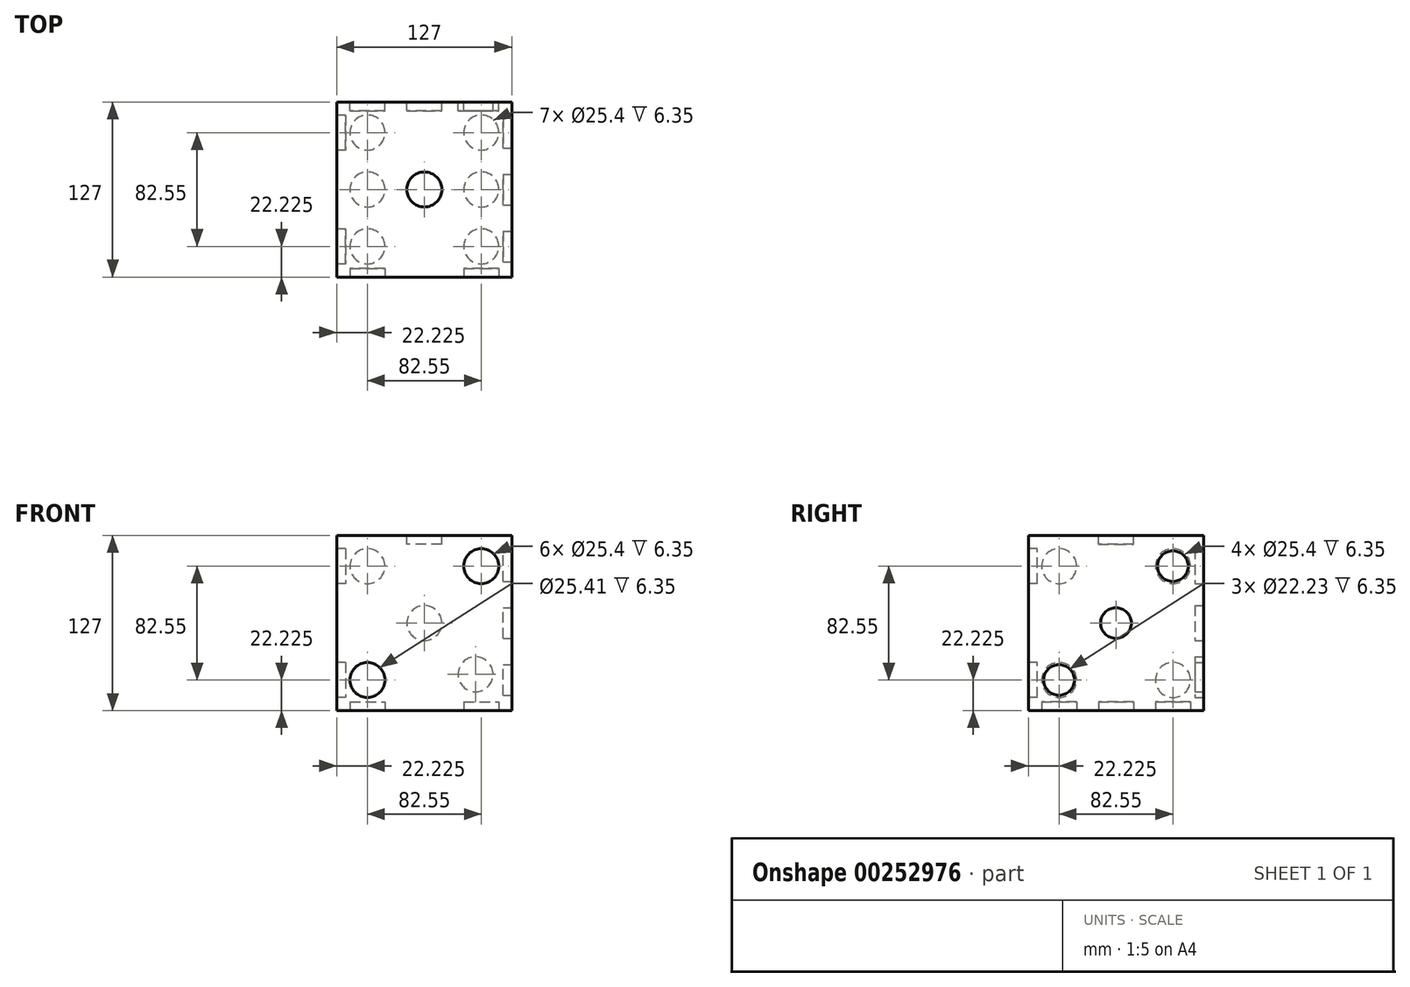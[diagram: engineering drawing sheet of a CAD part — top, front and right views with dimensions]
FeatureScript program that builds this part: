
annotation { "Feature Type Name" : "Feature", "Feature Type Description" : "" }
export const myFeature = defineFeature(function(context is Context, id is Id, definition is map)
    precondition{}
    {
        {
            var Q0;
            Q0=qCreatedBy(makeId("Top.planeOp"),FACE);
            var sketch = newSketch(context, id + "F0", { "sketchPlane" : qUnion([Q0])});
            skLineSegment(sketch, "E0.bottom", {"start": v(63.5, -63.5) * mm, "end": v(-63.5, -63.5) * mm});
            skLineSegment(sketch, "E0.top", {"start": v(63.5, 63.5) * mm, "end": v(-63.5, 63.5) * mm});
            skLineSegment(sketch, "E0.left", {"start": v(63.5, -63.5) * mm, "end": v(63.5, 63.5) * mm});
            skLineSegment(sketch, "E0.right", {"start": v(-63.5, -63.5) * mm, "end": v(-63.5, 63.5) * mm});
            skPoint(sketch, "E0.middle", {"position": v(0, 0) * mm});
            skSolve(sketch);
        }
        {
            var Q0;
            Q0 = qSketchRegion(id + "F0", true);
            extrude(context, id + "F1", {"entities" : qUnion([Q0]), "depth" : 127 * mm});
        }
        {
            var Q0;
            Q0=makeQuery(id+"F1.opExtrude","CAP_FACE",FACE,{"disambiguationData":[OSD([sQuery(id+"F0.wireOp",EDGE,"E0.bottom"),sQuery(id+"F0.wireOp",EDGE,"E0.top"),sQuery(id+"F0.wireOp",EDGE,"E0.left"),sQuery(id+"F0.wireOp",EDGE,"E0.right")])],"isStart":false});
            var sketch = newSketch(context, id + "F2", { "sketchPlane" : qUnion([Q0])});
            skCircle(sketch, "E1", {"center": v(0, 0) * mm, "radius": 12.7 * mm});
            skSolve(sketch);
        }
        {
            var Q0;
            Q0 = qSketchRegion(id + "F2", true);
            extrude(context, id + "F3", {"entities" : qUnion([Q0]), "operationType" : NewBodyOperationType.REMOVE, "oppositeDirection" : true, "depth" : 6.35 * mm});
        }
        {
            var Q0;
            Q0=makeQuery(id+"F1.opExtrude","SWEPT_FACE",FACE,{"disambiguationData":[OSD([sQuery(id+"F0.wireOp",EDGE,"E0.bottom")])]});
            var sketch = newSketch(context, id + "F4", { "sketchPlane" : qUnion([Q0])});
            skLineSegment(sketch, "E2", {"start": v(63.5, 127) * mm, "end": v(-63.5, 0) * mm, "construction": true});
            skCircle(sketch, "E3", {"center": v(-41.28, 22.23) * mm, "radius": 12.7 * mm});
            skCircle(sketch, "E4", {"center": v(41.27, 104.78) * mm, "radius": 12.7 * mm});
            skSolve(sketch);
        }
        {
            var Q0;
            Q0 = qSketchRegion(id + "F4", true);
            extrude(context, id + "F5", {"entities" : qUnion([Q0]), "operationType" : NewBodyOperationType.REMOVE, "oppositeDirection" : true, "depth" : 6.35 * mm});
        }
        {
            var Q0;
            Q0=makeQuery(id+"F1.opExtrude","SWEPT_FACE",FACE,{"disambiguationData":[OSD([sQuery(id+"F0.wireOp",EDGE,"E0.left")])]});
            var sketch = newSketch(context, id + "F6", { "sketchPlane" : qUnion([Q0])});
            skLineSegment(sketch, "E5", {"start": v(63.5, 127) * mm, "end": v(-63.5, 0) * mm, "construction": true});
            skCircle(sketch, "E6", {"center": v(-41.27, 22.23) * mm, "radius": 11.11 * mm});
            skCircle(sketch, "E7", {"center": v(41.28, 104.78) * mm, "radius": 11.11 * mm});
            skCircle(sketch, "E8", {"center": v(0, 63.5) * mm, "radius": 11.11 * mm});
            skSolve(sketch);
        }
        {
            var Q0;
            Q0 = qSketchRegion(id + "F6", true);
            extrude(context, id + "F7", {"entities" : qUnion([Q0]), "operationType" : NewBodyOperationType.REMOVE, "oppositeDirection" : true, "depth" : 6.35 * mm});
        }
        {
            var Q0;
            Q0=makeQuery(id+"F1.opExtrude","SWEPT_FACE",FACE,{"disambiguationData":[OSD([sQuery(id+"F0.wireOp",EDGE,"E0.right")])]});
            var sketch = newSketch(context, id + "F8", { "sketchPlane" : qUnion([Q0])});
            skLineSegment(sketch, "E9", {"start": v(63.5, 127) * mm, "end": v(-63.5, 0) * mm, "construction": true});
            skLineSegment(sketch, "E10", {"start": v(-63.5, 127) * mm, "end": v(63.5, 0) * mm, "construction": true});
            skCircle(sketch, "E11", {"center": v(-41.27, 22.23) * mm, "radius": 12.7 * mm});
            skCircle(sketch, "E12", {"center": v(41.27, 22.23) * mm, "radius": 12.7 * mm});
            skCircle(sketch, "E13", {"center": v(41.27, 104.77) * mm, "radius": 12.7 * mm});
            skCircle(sketch, "E14", {"center": v(-41.27, 104.77) * mm, "radius": 12.7 * mm});
            skSolve(sketch);
        }
        {
            var Q0;
            Q0 = qSketchRegion(id + "F8", true);
            extrude(context, id + "F9", {"entities" : qUnion([Q0]), "operationType" : NewBodyOperationType.REMOVE, "oppositeDirection" : true, "depth" : 6.35 * mm});
        }
        {
            var Q0;
            Q0=makeQuery(id+"F1.opExtrude","SWEPT_FACE",FACE,{"disambiguationData":[OSD([sQuery(id+"F0.wireOp",EDGE,"E0.top")])]});
            var sketch = newSketch(context, id + "F10", { "sketchPlane" : qUnion([Q0])});
            skLineSegment(sketch, "E15", {"start": v(63.5, 127) * mm, "end": v(-63.5, 0) * mm, "construction": true});
            skLineSegment(sketch, "E16", {"start": v(-63.5, 127) * mm, "end": v(63.5, 0) * mm, "construction": true});
            skCircle(sketch, "E17", {"center": v(-41.28, 104.78) * mm, "radius": 12.7 * mm});
            skCircle(sketch, "E18", {"center": v(41.27, 104.78) * mm, "radius": 12.7 * mm});
            skCircle(sketch, "E19", {"center": v(41.27, 22.23) * mm, "radius": 12.7 * mm});
            skCircle(sketch, "E20", {"center": v(-37.14, 26.36) * mm, "radius": 12.7 * mm});
            skCircle(sketch, "E21", {"center": v(0, 63.5) * mm, "radius": 12.7 * mm});
            skSolve(sketch);
        }
        {
            var Q0;
            Q0 = qSketchRegion(id + "F10", true);
            extrude(context, id + "F11", {"entities" : qUnion([Q0]), "operationType" : NewBodyOperationType.REMOVE, "oppositeDirection" : true, "depth" : 6.35 * mm});
        }
        {
            var Q0;
            Q0=makeQuery(id+"F1.opExtrude","CAP_FACE",FACE,{"disambiguationData":[OSD([sQuery(id+"F0.wireOp",EDGE,"E0.bottom"),sQuery(id+"F0.wireOp",EDGE,"E0.top"),sQuery(id+"F0.wireOp",EDGE,"E0.left"),sQuery(id+"F0.wireOp",EDGE,"E0.right")])],"isStart":true});
            var sketch = newSketch(context, id + "F12", { "sketchPlane" : qUnion([Q0])});
            skLineSegment(sketch, "E22", {"start": v(63.5, 63.5) * mm, "end": v(-63.5, -63.5) * mm, "construction": true});
            skLineSegment(sketch, "E23", {"start": v(-63.5, 63.5) * mm, "end": v(63.5, -63.5) * mm, "construction": true});
            skLineSegment(sketch, "E24", {"start": v(-63.5, 0) * mm, "end": v(63.5, 0) * mm, "construction": true});
            skCircle(sketch, "E25", {"center": v(-41.27, 41.27) * mm, "radius": 12.7 * mm});
            skCircle(sketch, "E26", {"center": v(41.28, 41.28) * mm, "radius": 12.7 * mm});
            skCircle(sketch, "E27", {"center": v(-41.27, 0) * mm, "radius": 12.7 * mm});
            skCircle(sketch, "E28", {"center": v(-41.27, -41.27) * mm, "radius": 12.7 * mm});
            skCircle(sketch, "E29", {"center": v(41.28, 0) * mm, "radius": 12.7 * mm});
            skCircle(sketch, "E30", {"center": v(41.28, -41.28) * mm, "radius": 12.7 * mm});
            skSolve(sketch);
        }
        {
            var Q0;
            Q0 = qSketchRegion(id + "F12", true);
            extrude(context, id + "F13", {"entities" : qUnion([Q0]), "operationType" : NewBodyOperationType.REMOVE, "oppositeDirection" : true, "depth" : 6.35 * mm});
        }
    });
